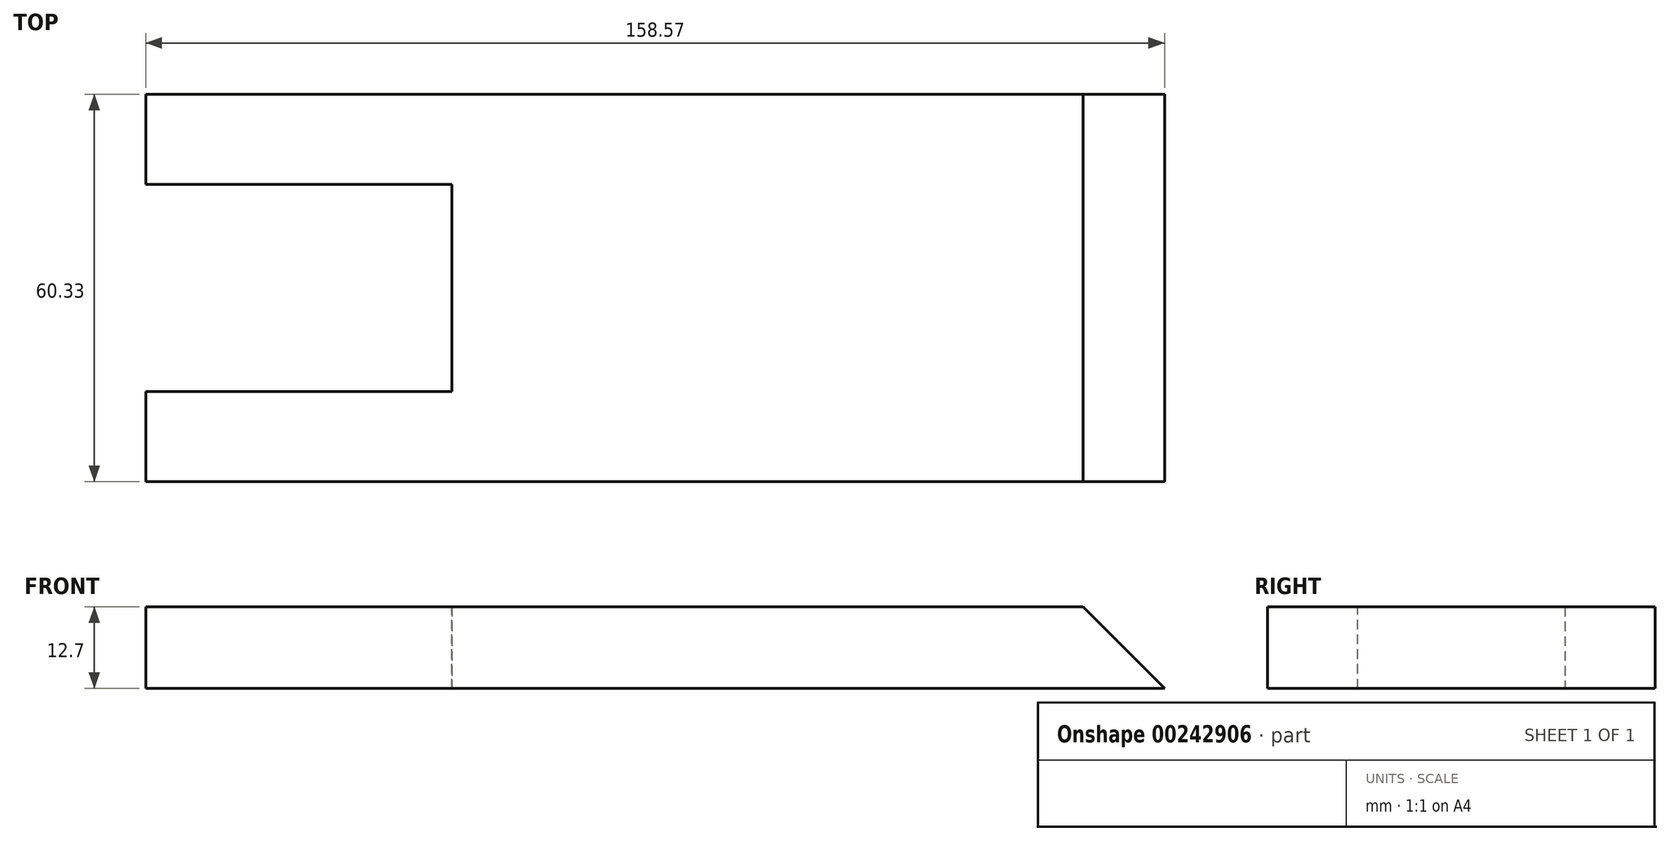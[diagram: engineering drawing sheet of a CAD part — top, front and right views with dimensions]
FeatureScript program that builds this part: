
annotation { "Feature Type Name" : "Feature", "Feature Type Description" : "" }
export const myFeature = defineFeature(function(context is Context, id is Id, definition is map)
    precondition{}
    {
        {
            var Q0;
            Q0=qCreatedBy(makeId("Top.planeOp"),FACE);
            var sketch = newSketch(context, id + "F0", { "sketchPlane" : qUnion([Q0])});
            skLineSegment(sketch, "E0", {"start": v(0, 0) * mm, "end": v(0, 14.3) * mm});
            skLineSegment(sketch, "E1", {"start": v(0, 14.3) * mm, "end": v(47.63, 14.3) * mm});
            skLineSegment(sketch, "E2", {"start": v(47.63, 14.3) * mm, "end": v(47.63, 46.04) * mm});
            skLineSegment(sketch, "E3", {"start": v(47.63, 46.04) * mm, "end": v(0, 46.04) * mm});
            skLineSegment(sketch, "E4", {"start": v(0, 46.04) * mm, "end": v(0, 60.33) * mm});
            skLineSegment(sketch, "E5", {"start": v(0, 60.33) * mm, "end": v(158.57, 60.33) * mm});
            skLineSegment(sketch, "E6", {"start": v(158.57, 60.33) * mm, "end": v(158.57, 0) * mm});
            skLineSegment(sketch, "E7", {"start": v(158.57, 0) * mm, "end": v(0, 0) * mm});
            skSolve(sketch);
        }
        {
            var Q0;
            Q0=qSketchRegion(id+"F0",true);
            extrude(context, id + "F1", {"entities" : qUnion([Q0]), "depth" : 12.7 * mm});
        }
        {
            var Q0;
            Q0=makeQuery(id+"F1.opExtrude","SWEPT_FACE",FACE,{"disambiguationData":[OSD([sQuery(id+"F0.wireOp",EDGE,"E5")])]});
            var sketch = newSketch(context, id + "F2", { "sketchPlane" : qUnion([Q0])});
            skLineSegment(sketch, "E8", {"start": v(-158.57, 0) * mm, "end": v(-145.87, 12.7) * mm});
            skLineSegment(sketch, "E9", {"start": v(-145.87, 12.7) * mm, "end": v(-158.57, 12.7) * mm});
            skLineSegment(sketch, "E10", {"start": v(-158.57, 12.7) * mm, "end": v(-158.57, 0) * mm});
            skSolve(sketch);
        }
        {
            var Q0;
            Q0=makeQuery(id+"F2.imprint","IMPRINT",FACE,{"disambiguationData":[TD([[makeQuery(id+"F2.imprint","IMPRINT",EDGE,{"derivedFrom":sQuery(id+"F2.wireOp",EDGE,"E8")}),1.0]])]});
            extrude(context, id + "F3", {"entities" : qUnion([Q0]), "operationType" : NewBodyOperationType.REMOVE, "oppositeDirection" : true, "depth" : 76.2 * mm});
        }
        {
            var Q0;
            Q0=makeQuery(id+"F1.opExtrude","SWEPT_FACE",FACE,{"disambiguationData":[OSD([sQuery(id+"F0.wireOp",EDGE,"E4")])]});
            var sketch = newSketch(context, id + "F4", { "sketchPlane" : qUnion([Q0])});
            skLineSegment(sketch, "E11", {"start": v(-46.04, 0) * mm, "end": v(-46.04, 12.7) * mm});
            skLineSegment(sketch, "E12", {"start": v(-46.04, 12.7) * mm, "end": v(-46.3, 12.7) * mm});
            skLineSegment(sketch, "E13", {"start": v(-46.3, 12.7) * mm, "end": v(-46.3, 0) * mm});
            skLineSegment(sketch, "E14", {"start": v(-46.3, 0) * mm, "end": v(-46.04, 0) * mm});
            skSolve(sketch);
        }
        {
            var Q0;
            Q0=makeQuery(id+"F4.imprint","IMPRINT",FACE,{"disambiguationData":[TD([[makeQuery(id+"F4.imprint","IMPRINT",EDGE,{"derivedFrom":sQuery(id+"F4.wireOp",EDGE,"E11")}),-1.0]])]});
            extrude(context, id + "F5", {"entities" : qUnion([Q0]), "operationType" : NewBodyOperationType.REMOVE, "oppositeDirection" : true, "depth" : 47.62 * mm});
        }
        {
            var Q0;
            Q0=makeQuery(id+"F1.opExtrude","SWEPT_FACE",FACE,{"disambiguationData":[OSD([sQuery(id+"F0.wireOp",EDGE,"E0")])]});
            var sketch = newSketch(context, id + "F6", { "sketchPlane" : qUnion([Q0])});
            skLineSegment(sketch, "E15", {"start": v(-14.3, 0) * mm, "end": v(-14.04, 0) * mm});
            skLineSegment(sketch, "E16", {"start": v(-14.04, 0) * mm, "end": v(-14.04, 12.7) * mm});
            skLineSegment(sketch, "E17", {"start": v(-14.04, 12.7) * mm, "end": v(-14.3, 12.7) * mm});
            skLineSegment(sketch, "E18", {"start": v(-14.3, 12.7) * mm, "end": v(-14.3, 0) * mm});
            skSolve(sketch);
        }
        {
            var Q0;
            Q0=makeQuery(id+"F6.imprint","IMPRINT",FACE,{"disambiguationData":[TD([[makeQuery(id+"F6.imprint","IMPRINT",EDGE,{"derivedFrom":sQuery(id+"F6.wireOp",EDGE,"E15")}),-1.0]])]});
            extrude(context, id + "F7", {"entities" : qUnion([Q0]), "operationType" : NewBodyOperationType.REMOVE, "oppositeDirection" : true, "depth" : 47.62 * mm});
        }
    });
